# Revit family: Paper_Towel_Dispenser_Hand_Dryer_Waste_Bin-Bobrick-TrimLineSeries-B-38031_Series
name_source: partatom
category: Specialty Equipment
units: mm (PartAtom-declared; Revit-internal decimal feet)

## family parameters
Cut with Voids When Loaded = No
Host = Face
OmniClass Number = 23.40.20.21.17
OmniClass Title = Paper Towel Dispensers, Disposal Units
Part Type = Normal
Room Calculation Point = No
Round Connector Dimension = Use Diameter
Shared = Yes

## types (2) — shared parameters
Assembly Code = C1030200
Default Elevation = 0"
Depth = 8 1/2"
Description = Paper Towel Dispenser/Hand Dryer/Waste Bin (3-in-1 Unit)
Dispense Capacity = Dispenses 600 multi-fold or 450 C-fold paper towels.
Finish = Stainless Steel-Gamco-#4 Satin
Height = 57 1/16"
Installation Type = Rcessed Wall Mounted
Manufacturer = Bobrick
Material = Stainless Steel-Bobrick-Satin
Mounting Height = 40"
Mounting Height Constraint = 40"
Product Documentation Link = https://www.bobrick.com
Product Page URL = https://www.bobrick.com
Rough Wall Opening Depth = 8"
Rough Wall Opening Height = 55 9/16"
Rough Wall Opening Width = 14 1/4"
Skirt Material = Stainless Steel-Bobrick-Satin
TowelMate Towel Rod Assembly Material = Nylon-Bobrick
URL = http://www.bobrick.com
Warranty Information = 1-Year Limited Warranty
Waste Capacity = 7.2-gal (27.4-L)
Waste Container Material = Plastic-Bobrick-Black
Width = 15 5/8"

## per-type parameters (varying)
| type | Cabinet Material | Door Material | Paper Towel Dispenser Material | Type Comments |
| B-38031 115V | Metal-Bobrick-Stainless Steel | Stainless Steel-Bobrick-Satin | Stainless Steel-Bobrick-Satin | Automatic Hand Dryer: 110-120V AC, 8.0 Amp, 920 Watts, 50/60 Hz, Single Phase, CUListed |
| B-38031 230V | Stainless Steel-Bobrick-Satin | Metal-Bobrick-Stainless Steel | Metal-Bobrick-Stainless Steel | Automatic Hand Dryer: 208-240V AC, 3.6-4.0 Amp, 750-950 Watts, 50/60 Hz, Single Phase, CE marked, CUListed, Meets Electrical Safety Requirement AS/NZS 600335 |

note: column(s) folded — value = type name in every type: Model

## geometry (parser evidence)
native form markers: Sweep x3
no freeform markers — native parametric forms only
